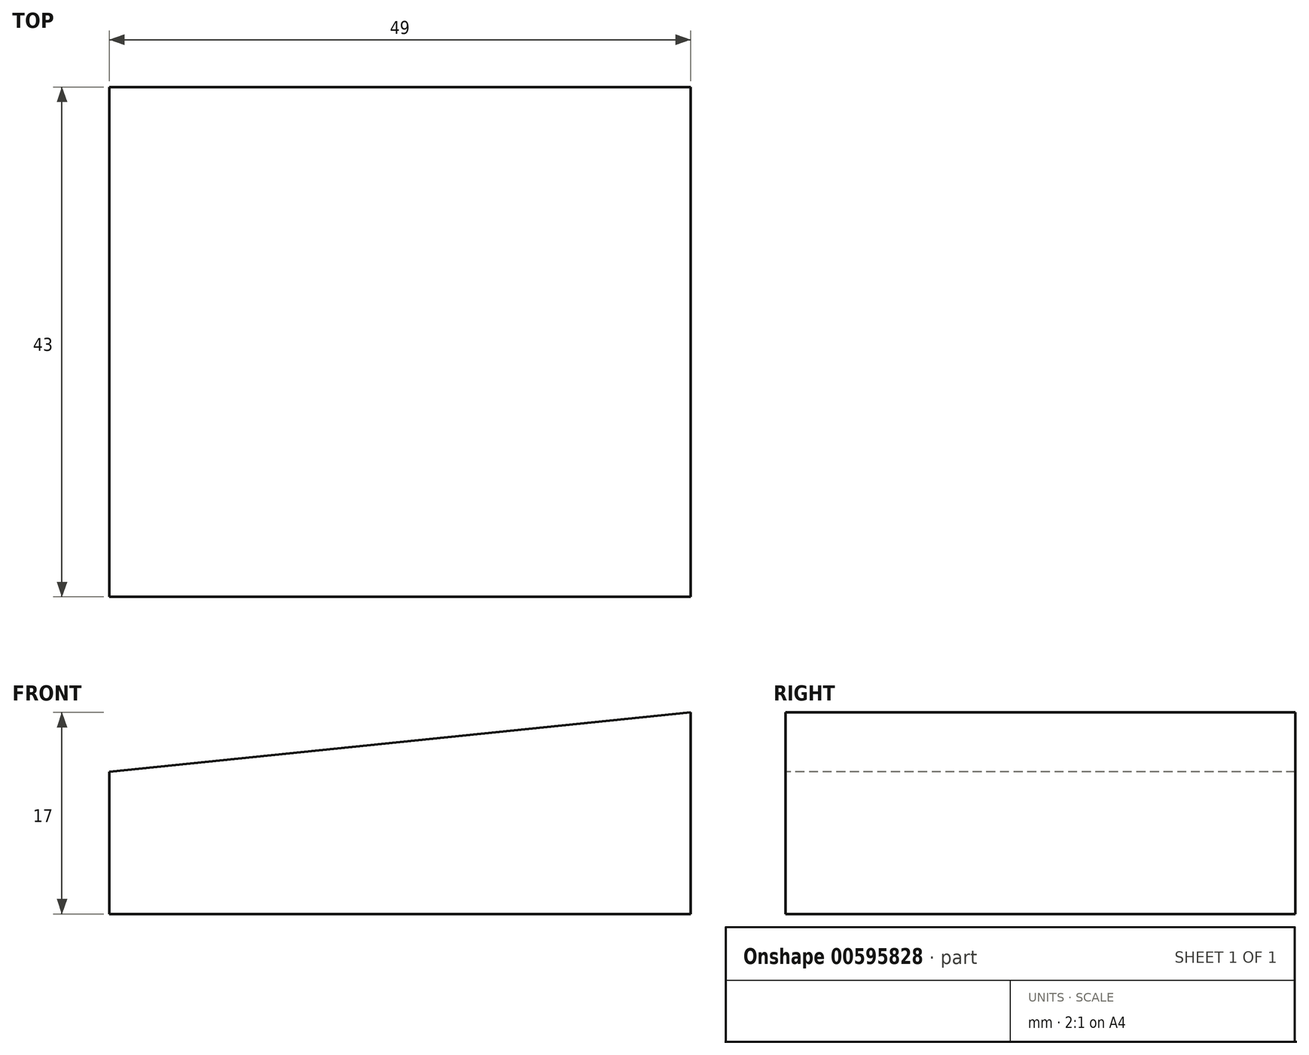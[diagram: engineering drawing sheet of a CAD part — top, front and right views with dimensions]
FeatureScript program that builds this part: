
annotation { "Feature Type Name" : "Feature", "Feature Type Description" : "" }
export const myFeature = defineFeature(function(context is Context, id is Id, definition is map)
    precondition{}
    {
        {
            var Q0;
            Q0=qCreatedBy(makeId("Top.planeOp"),FACE);
            var sketch = newSketch(context, id + "F0", { "sketchPlane" : qUnion([Q0])});
            skLineSegment(sketch, "E0.bottom", {"start": v(24.5, 21.5) * mm, "end": v(-24.5, 21.5) * mm});
            skLineSegment(sketch, "E0.top", {"start": v(24.5, -21.5) * mm, "end": v(-24.5, -21.5) * mm});
            skLineSegment(sketch, "E0.left", {"start": v(24.5, 21.5) * mm, "end": v(24.5, -21.5) * mm});
            skLineSegment(sketch, "E0.right", {"start": v(-24.5, 21.5) * mm, "end": v(-24.5, -21.5) * mm});
            skPoint(sketch, "E0.middle", {"position": v(0, 0) * mm});
            skSolve(sketch);
        }
        {
            var Q0;
            Q0=makeQuery(id+"F0.imprint","IMPRINT",FACE,{"disambiguationData":[TD([[makeQuery(id+"F0.imprint","IMPRINT",EDGE,{"derivedFrom":sQuery(id+"F0.wireOp",EDGE,"E0.bottom")}),1.0]])]});
            extrude(context, id + "F1", {"entities" : qUnion([Q0]), "depth" : 17 * mm, "offsetDistance" : 25 * mm});
        }
        {
            var Q0;
            Q0=makeQuery(id+"F1.opExtrude","SWEPT_FACE",FACE,{"disambiguationData":[OSD([sQuery(id+"F0.wireOp",EDGE,"E0.top")])]});
            var sketch = newSketch(context, id + "F2", { "sketchPlane" : qUnion([Q0])});
            skPoint(sketch, "E1", {"position": v(-24.5, 12) * mm});
            skLineSegment(sketch, "E2", {"start": v(24.5, 17) * mm, "end": v(-24.5, 12) * mm});
            skPoint(sketch, "E3", {"position": v(-24.5, 17) * mm});
            skLineSegment(sketch, "E4", {"start": v(-24.5, 17) * mm, "end": v(-24.5, 12) * mm});
            skLineSegment(sketch, "E5", {"start": v(-24.5, 17) * mm, "end": v(24.5, 17) * mm});
            skSolve(sketch);
        }
        {
            var Q0;
            Q0=makeQuery(id+"F2.imprint","IMPRINT",FACE,{"disambiguationData":[TD([[makeQuery(id+"F2.imprint","IMPRINT",EDGE,{"derivedFrom":sQuery(id+"F2.wireOp",EDGE,"E2")}),-1.0]])]});
            extrude(context, id + "F3", {"entities" : qUnion([Q0]), "operationType" : NewBodyOperationType.REMOVE, "endBound" : BoundingType.UP_TO_NEXT, "oppositeDirection" : true, "depth" : 25 * mm, "offsetDistance" : 25 * mm});
        }
    });
